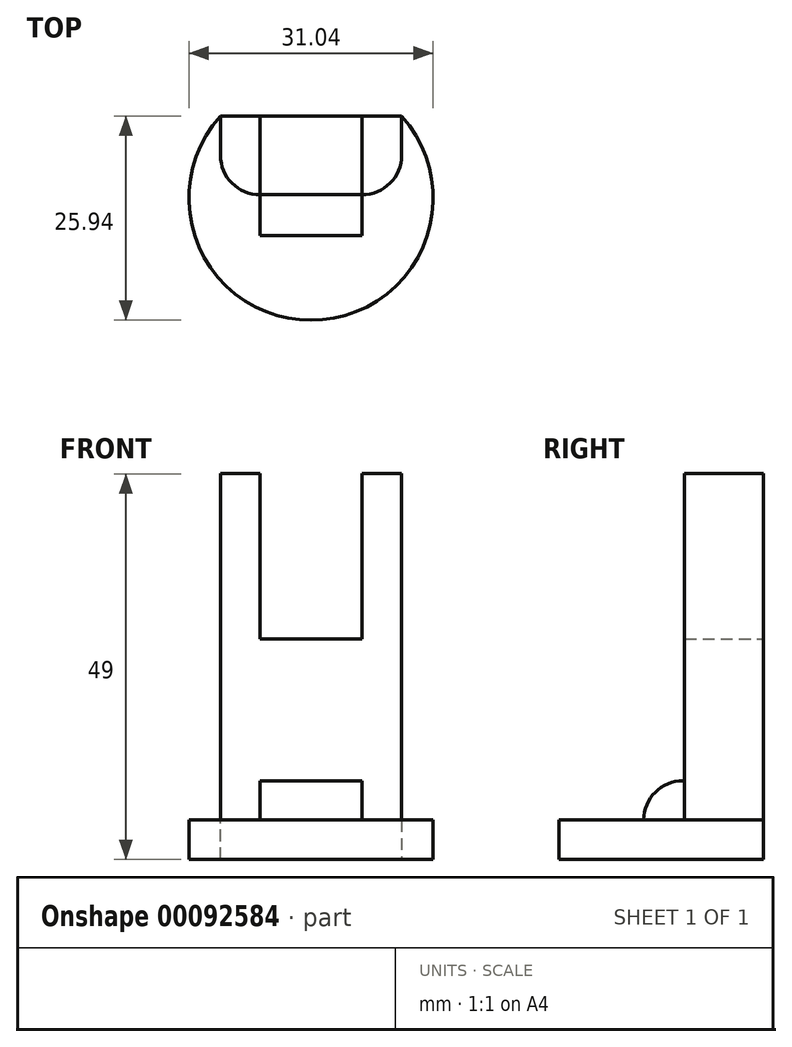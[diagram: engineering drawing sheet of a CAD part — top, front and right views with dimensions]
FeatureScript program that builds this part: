
annotation { "Feature Type Name" : "Feature", "Feature Type Description" : "" }
export const myFeature = defineFeature(function(context is Context, id is Id, definition is map)
    precondition{}
    {
        {
            var Q0;
            Q0=qCreatedBy(makeId("Front.planeOp"),FACE);
            var sketch = newSketch(context, id + "F0", { "sketchPlane" : qUnion([Q0])});
            skLineSegment(sketch, "E0", {"start": v(-15.94, 42.76) * mm, "end": v(-10.94, 42.76) * mm});
            skLineSegment(sketch, "E1", {"start": v(-10.94, 42.76) * mm, "end": v(-10.94, 21.76) * mm});
            skLineSegment(sketch, "E2", {"start": v(-10.94, 21.76) * mm, "end": v(2.06, 21.76) * mm});
            skLineSegment(sketch, "E3", {"start": v(2.06, 21.76) * mm, "end": v(2.06, 42.76) * mm});
            skLineSegment(sketch, "E4", {"start": v(2.06, 42.76) * mm, "end": v(7.06, 42.76) * mm});
            skLineSegment(sketch, "E5", {"start": v(7.06, 42.76) * mm, "end": v(7.06, -6.24) * mm});
            skLineSegment(sketch, "E6", {"start": v(7.06, -6.24) * mm, "end": v(-15.94, -6.24) * mm});
            skLineSegment(sketch, "E7", {"start": v(-15.94, -6.24) * mm, "end": v(-15.94, 42.76) * mm});
            skSolve(sketch);
        }
        {
            var Q0;
            Q0=makeQuery(id+"F0.imprint","IMPRINT",FACE,{"disambiguationData":[TD([[makeQuery(id+"F0.imprint","IMPRINT",EDGE,{"derivedFrom":sQuery(id+"F0.wireOp",EDGE,"E0")}),-1.0]])]});
            extrude(context, id + "F1", {"entities" : qUnion([Q0]), "depth" : 10 * mm});
        }
        {
            var Q0;
            Q0=makeQuery(id+"F1.opExtrude","SWEPT_FACE",FACE,{"disambiguationData":[OSD([sQuery(id+"F0.wireOp",EDGE,"E6")])]});
            var sketch = newSketch(context, id + "F2", { "sketchPlane" : qUnion([Q0])});
            skArc(sketch, "E8", {"start": v(7.06, 0) * mm, "mid": v(-4.44, 25.94) * mm, "end": v(-15.94, 0) * mm});
            skSolve(sketch);
        }
        {
            var Q0;
            Q0=makeQuery(id+"F2.imprint","IMPRINT",FACE,{"disambiguationData":[TD([[makeQuery(id+"F2.imprint","IMPRINT",EDGE,{"derivedFrom":sQuery(id+"F2.wireOp",EDGE,"E8")}),1.0]])]});
            extrude(context, id + "F3", {"entities" : qUnion([Q0]), "operationType" : NewBodyOperationType.ADD, "oppositeDirection" : true, "depth" : 5 * mm});
        }
        {
            var Q0;
            Q0=makeQuery(id+"F1.opExtrude","CAP_EDGE",EDGE,{"disambiguationData":[OSD([sQuery(id+"F0.wireOp",EDGE,"E7")])],"isStart":false});
            var Q1;
            Q1=makeQuery(id+"F1.opExtrude","CAP_EDGE",EDGE,{"disambiguationData":[OSD([sQuery(id+"F0.wireOp",EDGE,"E5")])],"isStart":false});
            fillet(context, id + "F4", {"entities" : qUnion([Q0, Q1]), "radius" : 5 * mm, "tangentPropagation" : true, "allowEdgeOverflow" : false});
        }
        {
            var Q0;
            Q0=makeQuery(id+"F3.opExtrude","CAP_FACE",FACE,{"disambiguationData":[OSD([sQuery(id+"F0.wireOp",EDGE,"E5"),sQuery(id+"F0.wireOp",EDGE,"E6"),sQuery(id+"F0.wireOp",EDGE,"E7"),sQuery(id+"F2.wireOp",EDGE,"E8")])],"isStart":false});
            var sketch = newSketch(context, id + "F5", { "sketchPlane" : qUnion([Q0])});
            skLineSegment(sketch, "E9", {"start": v(2.06, -10) * mm, "end": v(2.06, -15.2) * mm});
            skLineSegment(sketch, "E10", {"start": v(2.06, -15.2) * mm, "end": v(-10.94, -15.2) * mm});
            skLineSegment(sketch, "E11", {"start": v(-10.94, -15.2) * mm, "end": v(-10.94, -10) * mm});
            skLineSegment(sketch, "E12", {"start": v(-10.94, -10) * mm, "end": v(2.06, -10) * mm});
            skSolve(sketch);
        }
        {
            var Q0;
            Q0=makeQuery(id+"F5.imprint","IMPRINT",FACE,{"disambiguationData":[TD([[makeQuery(id+"F5.imprint","IMPRINT",EDGE,{"derivedFrom":sQuery(id+"F5.wireOp",EDGE,"E9")}),-1.0]])]});
            extrude(context, id + "F6", {"entities" : qUnion([Q0]), "operationType" : NewBodyOperationType.ADD, "depth" : 5 * mm});
        }
        {
            var Q0;
            Q0=makeQuery(id+"F6.opExtrude","CAP_EDGE",EDGE,{"disambiguationData":[OSD([sQuery(id+"F5.wireOp",EDGE,"E10")])],"isStart":false});
            fillet(context, id + "F7", {"entities" : qUnion([Q0]), "radius" : 5 * mm, "tangentPropagation" : true, "allowEdgeOverflow" : false});
        }
    });
